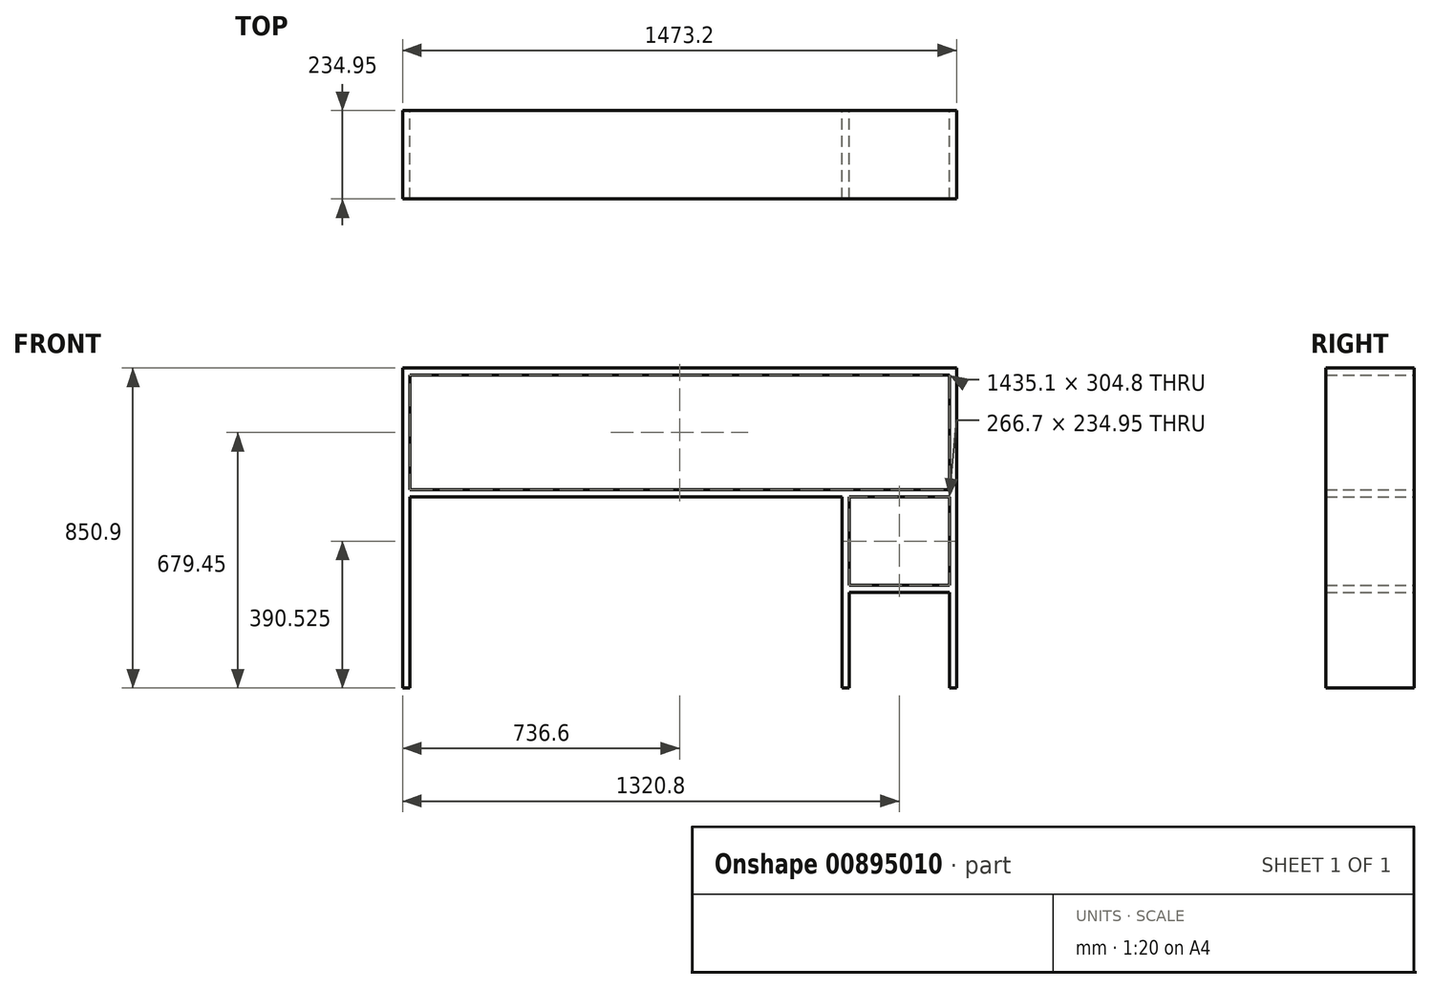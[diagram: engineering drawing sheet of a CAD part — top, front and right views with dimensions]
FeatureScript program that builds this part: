
annotation { "Feature Type Name" : "Feature", "Feature Type Description" : "" }
export const myFeature = defineFeature(function(context is Context, id is Id, definition is map)
    precondition{}
    {
        {
            var Q0;
            Q0=qCreatedBy(makeId("Front.planeOp"),FACE);
            var sketch = newSketch(context, id + "F0", { "sketchPlane" : qUnion([Q0])});
            skLineSegment(sketch, "E0.bottom", {"start": v(-736.6, 342.9) * mm, "end": v(736.6, 342.9) * mm});
            skLineSegment(sketch, "E0.top", {"start": v(-736.6, -508) * mm, "end": v(-717.55, -508) * mm});
            skLineSegment(sketch, "E0.left", {"start": v(-736.6, 342.9) * mm, "end": v(-736.6, -508) * mm});
            skLineSegment(sketch, "E0.right", {"start": v(736.6, 342.9) * mm, "end": v(736.6, -508) * mm});
            skLineSegment(sketch, "E1.top", {"start": v(717.55, 323.85) * mm, "end": v(-717.55, 323.85) * mm});
            skLineSegment(sketch, "E1.left", {"start": v(717.55, -508) * mm, "end": v(717.55, -254) * mm});
            skLineSegment(sketch, "E1.right", {"start": v(-717.55, -508) * mm, "end": v(-717.55, 0) * mm});
            skLineSegment(sketch, "E2.bottom", {"start": v(-717.55, 19.05) * mm, "end": v(717.55, 19.05) * mm});
            skLineSegment(sketch, "E2.top", {"start": v(-717.55, 0) * mm, "end": v(431.8, 0) * mm});
            skLineSegment(sketch, "E3.trimOffspring", {"start": v(717.55, 19.05) * mm, "end": v(717.55, 323.85) * mm});
            skLineSegment(sketch, "E4.trimOffspring", {"start": v(-717.55, 19.05) * mm, "end": v(-717.55, 323.85) * mm});
            skLineSegment(sketch, "E5.trimOffspring", {"start": v(717.55, -508) * mm, "end": v(736.6, -508) * mm});
            skLineSegment(sketch, "E6.top", {"start": v(431.8, -508) * mm, "end": v(450.85, -508) * mm});
            skLineSegment(sketch, "E6.left", {"start": v(431.8, 0) * mm, "end": v(431.8, -508) * mm});
            skLineSegment(sketch, "E6.right", {"start": v(450.85, 0) * mm, "end": v(450.85, -234.95) * mm});
            skLineSegment(sketch, "E7.bottom", {"start": v(450.85, -234.95) * mm, "end": v(717.55, -234.95) * mm});
            skLineSegment(sketch, "E7.top", {"start": v(450.85, -254) * mm, "end": v(717.55, -254) * mm});
            skLineSegment(sketch, "E8.trimOffspring", {"start": v(450.85, -254) * mm, "end": v(450.85, -508) * mm});
            skLineSegment(sketch, "E9.trimOffspring", {"start": v(717.55, -234.95) * mm, "end": v(717.55, 0) * mm});
            skLineSegment(sketch, "E10.trimOffspring", {"start": v(450.85, 0) * mm, "end": v(717.55, 0) * mm});
            skSolve(sketch);
        }
        {
            var Q0;
            Q0 = qSketchRegion(id + "F0", true);
            extrude(context, id + "F1", {"entities" : qUnion([Q0]), "depth" : 234.95 * mm, "offsetDistance" : 25.4 * mm});
        }
    });
